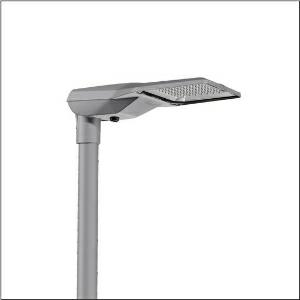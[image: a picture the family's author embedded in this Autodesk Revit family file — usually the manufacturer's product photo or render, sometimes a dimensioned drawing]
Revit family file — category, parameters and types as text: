
# Revit family: streetlight_sl_21_midi___p0_5a_5xe3v33r08mb_b2b8
name_source: partatom
category: Lighting Fixtures
units: mm (PartAtom-declared; Revit-internal decimal feet)

## family parameters
Cut with Voids When Loaded = No
Host = Face
Light Source = No
Part Type = Normal
Room Calculation Point = No
Round Connector Dimension = Use Diameter
Shared = No

## types (1)
- --- (1 x LED, 17960 lm, 136 W, 3000K)
    Apparent Load = 136 VA
    CIE Flux Codes = 37 73 96 100 100
    Color Rendering = 70
    Color Temperature = 3000K
    Default Elevation = 1800 mm
    Description = Streetlight SL 21 midi, mast luminaire, primary light control with lens, of PMMA, primary optical cover: cover, of toughened safety glass, transparent, light distribution: P0.5a, light emission: direct distribution, primary light characteristic: asymmetric, installation type: post-top, side-entry, LED, High Power LED, rated luminous flux: 17.960lm, luminous efficacy: 132lm/W, light colour: 730, colour temperature: 3000K, control gear: D4i, control: pre-setting: logarithmic dimming characteristic, flexible luminous flux parameterisation, time-dependent luminous flux control, constant luminous flux control, overheat protection, mains connection: 230..240V, AC, 50/60Hz, start of lifetime: 136W, end of service life: 142W, reduction: 61W, luminaire housing, of diecast aluminium, powder-coated, SITECO metallic grey (DB 702S), corrosivity category C5 high according to DIN EN ISO 12944, multi-level sealing system, sealing non-destructively replaceable, inclination adjustable: 0°, 5°, 10°, 15°, please order mast flange separately, length: 644mm, width: 335mm, height: 110mm, mast flange for spigot size: 42mm (side-entry): 5XC10008XM4, 60/48mm (side-entry/post-top): 5XC10108XM2, 76/60mm (side-entry/post-top): 5XC10108XM1, mounting height: 4..8m, Smart Interface below, protection rating (complete): IP66, insulation class (complete): insulation class II (safety insulation), certification: CE, ENEC, ENEC+, VDE, impact resistance: IK10, permissible operating ambient temperature for outdoor applications: -40..+50°C, standard-compliant lighting for roads and squares, packaging unit: 1 piece

Light Distribution: P0.5a
    Height = 111 mm
    Lamp = 1 x LED
    Lamp Light Flux = 17960 lm
    Lamp Power = 136 W
    Lamp count = 1
    Length = 644 mm
    Luminous efficacy = 132 lm/W
    Manufacturer = Siteco
    ModVariant = No
    Model = 5XE3V33R08MB
    Number of Poles = 1
    OnlyDefault = Yes
    Power Factor = 1
    Product Name = Streetlight SL 21 midi | P0.5a
    Product group = mast luminaire | pylon top
    ProductGroupID = 6100
    Protection Class = Protection class II
    Protection Degree = IP 66
    RLX_Detail_Level = 1
    RLX_Emergency_Light_Flux = 0 lm
    RLX_Emergency_Type = 0
    RLX_Emergency_Type_DB = No
    RlxData = <blob elided: 89961 chars, md5=ec1636a9>
    Socket = socket
    Standby Power = 0 W
    System Light Flux = 17960 lm
    System Power = 136 W
    Type Comments = factory setting: luminous flux: 100 % | dim-lin: 254 | 695 mA
    Type Image = l_1004300.jpg
    URL = http://relux.com
    VarID = @adj_077693
    Voltage = 0 V
    Weight = 0.00 kg
    Width = 336 mm

## geometry (parser evidence)
native form markers: Blend x4, Sweep x12
no freeform markers — native parametric forms only
